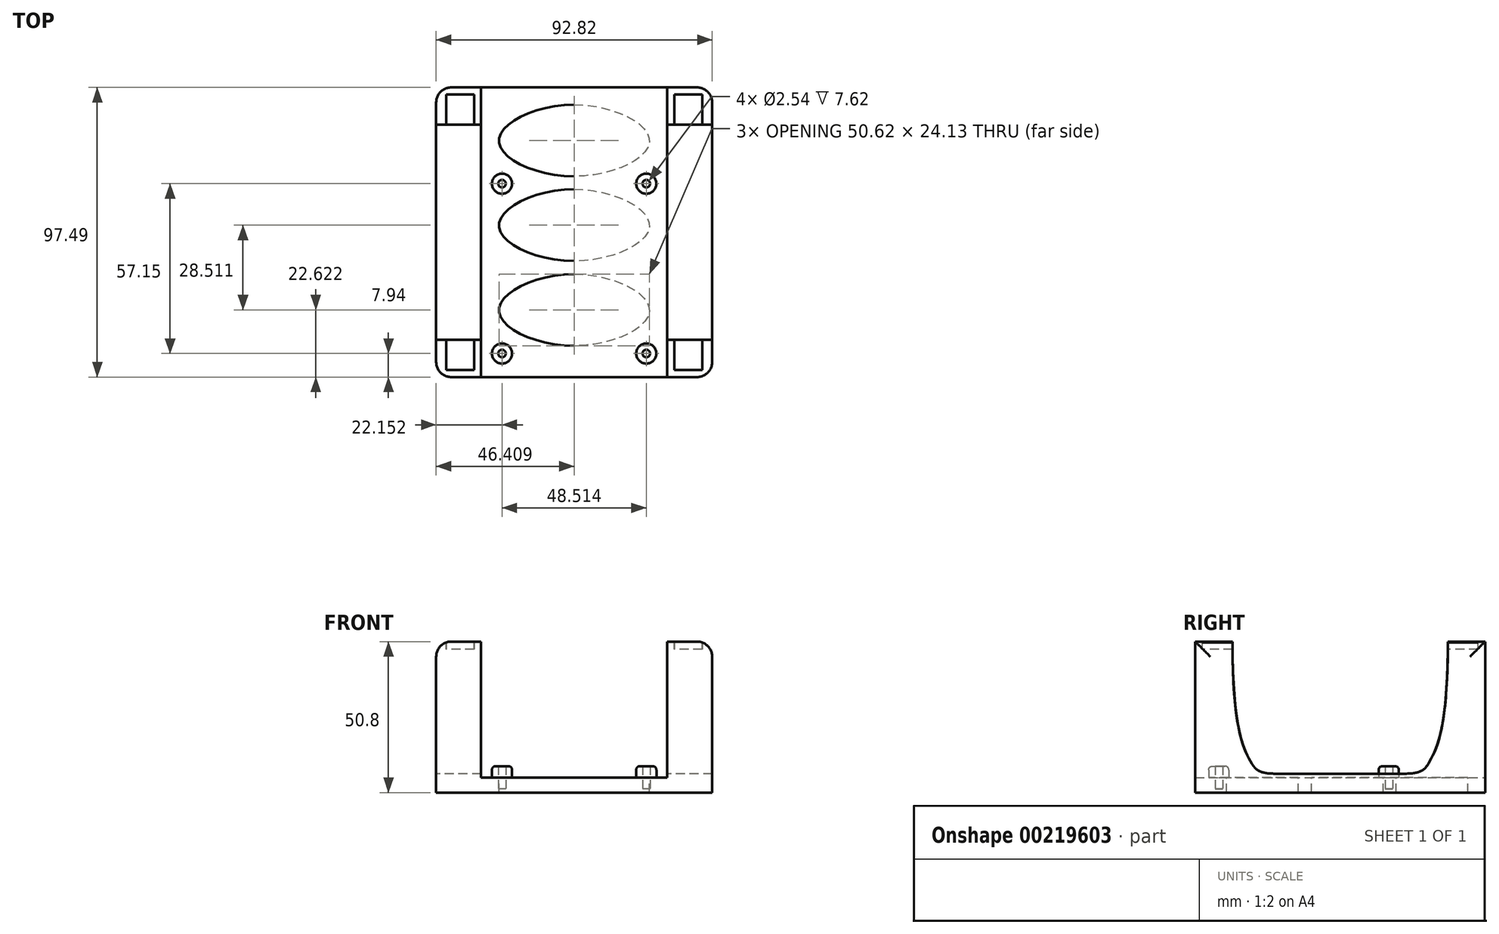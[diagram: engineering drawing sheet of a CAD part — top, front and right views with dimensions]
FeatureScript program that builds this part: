
annotation { "Feature Type Name" : "Feature", "Feature Type Description" : "" }
export const myFeature = defineFeature(function(context is Context, id is Id, definition is map)
    precondition{}
    {
        {
            var Q0;
            Q0=qCreatedBy(makeId("Top.planeOp"),FACE);
            var sketch = newSketch(context, id + "F0", { "sketchPlane" : qUnion([Q0])});
            skLineSegment(sketch, "E0.bottom", {"start": v(0, 8.91) * mm, "end": v(92.82, 8.91) * mm});
            skLineSegment(sketch, "E0.top", {"start": v(0, 106.4) * mm, "end": v(92.82, 106.4) * mm});
            skLineSegment(sketch, "E0.left", {"start": v(0, 8.91) * mm, "end": v(0, 106.4) * mm});
            skLineSegment(sketch, "E0.right", {"start": v(92.82, 8.91) * mm, "end": v(92.82, 106.4) * mm});
            skLineSegment(sketch, "E1.bottom", {"start": v(3.36, 104.01) * mm, "end": v(12.75, 104.01) * mm});
            skLineSegment(sketch, "E1.top", {"start": v(3.36, 11.3) * mm, "end": v(12.75, 11.3) * mm});
            skLineSegment(sketch, "E1.left", {"start": v(3.36, 104.01) * mm, "end": v(3.36, 11.3) * mm});
            skLineSegment(sketch, "E1.right", {"start": v(12.75, 104.01) * mm, "end": v(12.75, 11.3) * mm});
            skLineSegment(sketch, "E2", {"start": v(46.4, 106.4) * mm, "end": v(46.4, 8.91) * mm, "construction": true});
            skLineSegment(sketch, "E3", {"start": v(12.75, 11.3) * mm, "end": v(12.75, 8.91) * mm, "construction": true});
            skLineSegment(sketch, "E4", {"start": v(12.75, 104.01) * mm, "end": v(12.75, 106.4) * mm, "construction": true});
            skLineSegment(sketch, "E5.MirrorCS", {"start": v(89.46, 104.01) * mm, "end": v(80.06, 104.01) * mm});
            skLineSegment(sketch, "E6.MirrorCS", {"start": v(80.06, 104.01) * mm, "end": v(80.06, 11.3) * mm});
            skLineSegment(sketch, "E7.MirrorCS", {"start": v(89.46, 104.01) * mm, "end": v(89.46, 11.3) * mm});
            skLineSegment(sketch, "E8.MirrorCS", {"start": v(89.46, 11.3) * mm, "end": v(80.06, 11.3) * mm});
            skSolve(sketch);
        }
        {
            var Q0;
            Q0=makeQuery(id+"F0.imprint","IMPRINT",FACE,{"disambiguationData":[TD([[makeQuery(id+"F0.imprint","IMPRINT",EDGE,{"derivedFrom":sQuery(id+"F0.wireOp",EDGE,"E0.bottom")}),1.0]])]});
            var Q1;
            Q1=makeQuery(id+"F0.imprint","IMPRINT",FACE,{"disambiguationData":[TD([[makeQuery(id+"F0.imprint","IMPRINT",EDGE,{"derivedFrom":sQuery(id+"F0.wireOp",EDGE,"E1.bottom")}),-1.0]])]});
            var Q2;
            Q2=makeQuery(id+"F0.imprint","IMPRINT",FACE,{"disambiguationData":[TD([[makeQuery(id+"F0.imprint","IMPRINT",EDGE,{"derivedFrom":sQuery(id+"F0.wireOp",EDGE,"E5.MirrorCS")}),1.0]])]});
            extrude(context, id + "F1", {"entities" : qUnion([Q0, Q1, Q2]), "oppositeDirection" : true, "depth" : 50.8 * mm});
        }
        {
            var Q0;
            Q0=makeQuery(id+"F0.imprint","IMPRINT",FACE,{"disambiguationData":[TD([[makeQuery(id+"F0.imprint","IMPRINT",EDGE,{"derivedFrom":sQuery(id+"F0.wireOp",EDGE,"E1.bottom")}),-1.0]])]});
            var Q1;
            Q1=makeQuery(id+"F0.imprint","IMPRINT",FACE,{"disambiguationData":[TD([[makeQuery(id+"F0.imprint","IMPRINT",EDGE,{"derivedFrom":sQuery(id+"F0.wireOp",EDGE,"E5.MirrorCS")}),1.0]])]});
            extrude(context, id + "F2", {"entities" : qUnion([Q0, Q1]), "operationType" : NewBodyOperationType.REMOVE, "oppositeDirection" : true, "depth" : 2.54 * mm});
        }
        {
            var Q0;
            Q0=makeQuery(id+"F0.imprint","IMPRINT",FACE,{"disambiguationData":[TD([[makeQuery(id+"F0.imprint","IMPRINT",EDGE,{"derivedFrom":sQuery(id+"F0.wireOp",EDGE,"E0.bottom")}),1.0]])]});
            var sketch = newSketch(context, id + "F3", { "sketchPlane" : qUnion([Q0])});
            skLineSegment(sketch, "E9.bottom", {"start": v(77.71, 8.91) * mm, "end": v(15.1, 8.91) * mm});
            skLineSegment(sketch, "E9.top", {"start": v(77.71, 106.4) * mm, "end": v(15.1, 106.4) * mm});
            skLineSegment(sketch, "E9.left", {"start": v(77.71, 8.91) * mm, "end": v(77.71, 106.4) * mm});
            skLineSegment(sketch, "E9.right", {"start": v(15.1, 8.91) * mm, "end": v(15.1, 106.4) * mm});
            skPoint(sketch, "E9.middle", {"position": v(46.4, 57.66) * mm});
            skSolve(sketch);
        }
        {
            var Q0;
            Q0=makeQuery(id+"F3.imprint","IMPRINT",FACE,{"disambiguationData":[TD([[makeQuery(id+"F3.imprint","IMPRINT",EDGE,{"derivedFrom":sQuery(id+"F3.wireOp",EDGE,"E9.bottom")}),1.0]])]});
            extrude(context, id + "F4", {"entities" : qUnion([Q0]), "operationType" : NewBodyOperationType.REMOVE, "oppositeDirection" : true, "depth" : 45.72 * mm});
        }
        {
            var Q0;
            Q0=makeQuery(id+"F1.opExtrude","SWEPT_FACE",FACE,{"disambiguationData":[OSD([sQuery(id+"F0.wireOp",EDGE,"E0.left")])]});
            var sketch = newSketch(context, id + "F5", { "sketchPlane" : qUnion([Q0])});
            skPoint(sketch, "E10", {"position": v(-57.66, 0) * mm});
            skLineSegment(sketch, "E11", {"start": v(-93.85, 0) * mm, "end": v(-21.46, 0) * mm, "construction": true});
            skPoint(sketch, "E12", {"position": v(-104.01, 0) * mm});
            skFitSpline(sketch, "E13", {"points": [v(-93.85, 0) * mm, v(-87.7, -40.47) * mm, v(-79.46, -44.45) * mm], "startDerivative": vector(0, -127.08) * mm, "endDerivative": vector(55.42, 0) * mm});
            skLineSegment(sketch, "E14", {"start": v(-79.46, -44.45) * mm, "end": v(-57.66, -44.45) * mm});
            skLineSegment(sketch, "E15", {"start": v(-57.66, 0) * mm, "end": v(-57.66, -44.45) * mm, "construction": true});
            skLineSegment(sketch, "E16.MirrorCS", {"start": v(-35.86, -44.45) * mm, "end": v(-57.66, -44.45) * mm});
            skFitSpline(sketch, "E17.MirrorCS", {"points": [v(-21.46, 0) * mm, v(-27.62, -40.47) * mm, v(-35.86, -44.45) * mm], "startDerivative": vector(0, -127.08) * mm, "endDerivative": vector(-55.42, 0) * mm});
            skLineSegment(sketch, "E18", {"start": v(-93.85, 0) * mm, "end": v(-21.46, 0) * mm});
            skSolve(sketch);
        }
        {
            var Q0;
            {var subQ0=sQuery(id+"F5.wireOp",EDGE,"dd278821-00e8-4460-ae2d-502975557ae5");Q0=makeQuery(id+"F5.imprint","IMPRINT",FACE,{"disambiguationData":[TD([[makeQuery(id+"F5.imprint","IMPRINT",EDGE,{"derivedFrom":subQ0}),1.0]])]});}
            var Q1;
            Q1=makeQuery(id+"F5.imprint","IMPRINT",FACE,{"disambiguationData":[TD([[makeQuery(id+"F5.imprint","IMPRINT",EDGE,{"derivedFrom":sQuery(id+"F5.wireOp",EDGE,"E13")}),1.0]])]});
            extrude(context, id + "F6", {"entities" : qUnion([Q0, Q1]), "operationType" : NewBodyOperationType.REMOVE, "endBound" : BoundingType.THROUGH_ALL, "oppositeDirection" : true, "depth" : 25.4 * mm});
        }
        {
            var Q0;
            Q0=makeQuery(id+"F4.boolean.opBoolean","COPY",FACE,{"derivedFrom":makeQuery(id+"F4.opExtrude","CAP_FACE",FACE,{"disambiguationData":[OSD([sQuery(id+"F3.wireOp",EDGE,"E9.bottom"),sQuery(id+"F3.wireOp",EDGE,"E9.top"),sQuery(id+"F3.wireOp",EDGE,"E9.left"),sQuery(id+"F3.wireOp",EDGE,"E9.right")])],"isStart":false})});
            var sketch = newSketch(context, id + "F7", { "sketchPlane" : qUnion([Q0])});
            skLineSegment(sketch, "E19.bottom", {"start": v(18.34, 77.81) * mm, "end": v(74.48, 77.81) * mm});
            skLineSegment(sketch, "E19.top", {"start": v(18.34, -9.31) * mm, "end": v(74.48, -9.31) * mm});
            skLineSegment(sketch, "E19.left", {"start": v(18.34, 77.81) * mm, "end": v(18.34, -9.31) * mm});
            skLineSegment(sketch, "E19.right", {"start": v(74.48, 77.81) * mm, "end": v(74.48, -9.31) * mm});
            skCircle(sketch, "E20", {"center": v(22.15, 74) * mm, "radius": 1.27 * mm});
            skCircle(sketch, "E21", {"center": v(70.67, 74) * mm, "radius": 1.27 * mm});
            skLineSegment(sketch, "E22", {"start": v(22.15, 74) * mm, "end": v(70.67, 74) * mm, "construction": true});
            skLineSegment(sketch, "E23", {"start": v(22.15, 74) * mm, "end": v(18.34, 74) * mm, "construction": true});
            skLineSegment(sketch, "E24", {"start": v(70.67, 74) * mm, "end": v(74.48, 74) * mm, "construction": true});
            skLineSegment(sketch, "E25", {"start": v(70.67, 74) * mm, "end": v(70.67, 77.81) * mm, "construction": true});
            skCircle(sketch, "E26", {"center": v(70.67, 16.85) * mm, "radius": 1.27 * mm});
            skLineSegment(sketch, "E27", {"start": v(70.67, 74) * mm, "end": v(70.67, 16.85) * mm, "construction": true});
            skCircle(sketch, "E28", {"center": v(22.15, 16.85) * mm, "radius": 1.27 * mm});
            skPoint(sketch, "E29", {"position": v(46.4, 77.81) * mm});
            skCircle(sketch, "E30", {"center": v(70.67, 74) * mm, "radius": 3.4 * mm});
            skCircle(sketch, "E31", {"center": v(70.67, 16.85) * mm, "radius": 3.4 * mm});
            skCircle(sketch, "E32", {"center": v(22.15, 16.85) * mm, "radius": 3.4 * mm});
            skCircle(sketch, "E33", {"center": v(22.15, 74) * mm, "radius": 3.4 * mm});
            skSolve(sketch);
        }
        {
            var Q0;
            Q0=makeQuery(id+"F7.imprint","IMPRINT",FACE,{"disambiguationData":[TD([[makeQuery(id+"F7.imprint","IMPRINT",EDGE,{"derivedFrom":sQuery(id+"F7.wireOp",EDGE,"E21")}),-1.0]])]});
            var Q1;
            Q1=makeQuery(id+"F7.imprint","IMPRINT",FACE,{"disambiguationData":[TD([[makeQuery(id+"F7.imprint","IMPRINT",EDGE,{"derivedFrom":sQuery(id+"F7.wireOp",EDGE,"E20")}),-1.0]])]});
            var Q2;
            Q2=makeQuery(id+"F7.imprint","IMPRINT",FACE,{"disambiguationData":[TD([[makeQuery(id+"F7.imprint","IMPRINT",EDGE,{"derivedFrom":sQuery(id+"F7.wireOp",EDGE,"E28")}),-1.0]])]});
            var Q3;
            Q3=makeQuery(id+"F7.imprint","IMPRINT",FACE,{"disambiguationData":[TD([[makeQuery(id+"F7.imprint","IMPRINT",EDGE,{"derivedFrom":sQuery(id+"F7.wireOp",EDGE,"E26")}),-1.0]])]});
            extrude(context, id + "F8", {"entities" : qUnion([Q0, Q1, Q2, Q3]), "operationType" : NewBodyOperationType.ADD, "depth" : 3.8 * mm});
        }
        {
            var Q0;
            Q0=makeQuery(id+"F7.imprint","IMPRINT",FACE,{"disambiguationData":[TD([[makeQuery(id+"F7.imprint","IMPRINT",EDGE,{"derivedFrom":sQuery(id+"F7.wireOp",EDGE,"E21")}),1.0]])]});
            var Q1;
            Q1=makeQuery(id+"F7.imprint","IMPRINT",FACE,{"disambiguationData":[TD([[makeQuery(id+"F7.imprint","IMPRINT",EDGE,{"derivedFrom":sQuery(id+"F7.wireOp",EDGE,"E28")}),1.0]])]});
            var Q2;
            Q2=makeQuery(id+"F7.imprint","IMPRINT",FACE,{"disambiguationData":[TD([[makeQuery(id+"F7.imprint","IMPRINT",EDGE,{"derivedFrom":sQuery(id+"F7.wireOp",EDGE,"E20")}),1.0]])]});
            var Q3;
            Q3=makeQuery(id+"F7.imprint","IMPRINT",FACE,{"disambiguationData":[TD([[makeQuery(id+"F7.imprint","IMPRINT",EDGE,{"derivedFrom":sQuery(id+"F7.wireOp",EDGE,"E26")}),1.0]])]});
            extrude(context, id + "F9", {"entities" : qUnion([Q0, Q1, Q2, Q3]), "operationType" : NewBodyOperationType.REMOVE, "oppositeDirection" : true, "depth" : 3.8 * mm});
        }
        {
            var Q0;
            Q0=makeQuery(id+"F1.opExtrude","SWEPT_EDGE",EDGE,{"disambiguationData":[OSD([sQuery(id+"F0.wireOp",EDGE,"E0.bottom"),sQuery(id+"F0.wireOp",EDGE,"E0.left")])]});
            var Q1;
            Q1=makeQuery(id+"F1.opExtrude","SWEPT_EDGE",EDGE,{"disambiguationData":[OSD([sQuery(id+"F0.wireOp",EDGE,"E0.bottom"),sQuery(id+"F0.wireOp",EDGE,"E0.right")])]});
            var Q2;
            Q2=makeQuery(id+"F1.opExtrude","SWEPT_EDGE",EDGE,{"disambiguationData":[OSD([sQuery(id+"F0.wireOp",EDGE,"E0.top"),sQuery(id+"F0.wireOp",EDGE,"E0.left")])]});
            var Q3;
            Q3=makeQuery(id+"F1.opExtrude","SWEPT_EDGE",EDGE,{"disambiguationData":[OSD([sQuery(id+"F0.wireOp",EDGE,"E0.top"),sQuery(id+"F0.wireOp",EDGE,"E0.right")])]});
            var Q4;
            {var subQ0=sQuery(id+"F0.wireOp",EDGE,"E0.bottom");var subQ1=sQuery(id+"F0.wireOp",EDGE,"E0.left");Q4=makeQuery(id+"F6.boolean.opBoolean","SPLIT",EDGE,{"disambiguationData":[TD([makeQuery(id+"F1.opExtrude","SWEPT_FACE",FACE,{"disambiguationData":[OSD([subQ0])]})])],"derivedFrom":makeQuery(id+"F1.opExtrude","CAP_EDGE",EDGE,{"disambiguationData":[OSD([subQ1])],"isStart":true})});}
            var Q5;
            {var subQ0=sQuery(id+"F0.wireOp",EDGE,"E0.left");var subQ1=sQuery(id+"F0.wireOp",EDGE,"E0.top");Q5=makeQuery(id+"F6.boolean.opBoolean","SPLIT",EDGE,{"disambiguationData":[TD([makeQuery(id+"F1.opExtrude","SWEPT_FACE",FACE,{"disambiguationData":[OSD([subQ1])]})])],"derivedFrom":makeQuery(id+"F1.opExtrude","CAP_EDGE",EDGE,{"disambiguationData":[OSD([subQ0])],"isStart":true})});}
            var Q6;
            {var subQ0=sQuery(id+"F0.wireOp",EDGE,"E0.right");var subQ1=sQuery(id+"F0.wireOp",EDGE,"E0.top");Q6=makeQuery(id+"F6.boolean.opBoolean","SPLIT",EDGE,{"disambiguationData":[TD([makeQuery(id+"F1.opExtrude","SWEPT_FACE",FACE,{"disambiguationData":[OSD([subQ1])]})])],"derivedFrom":makeQuery(id+"F1.opExtrude","CAP_EDGE",EDGE,{"disambiguationData":[OSD([subQ0])],"isStart":true})});}
            var Q7;
            {var subQ0=sQuery(id+"F0.wireOp",EDGE,"E0.bottom");var subQ1=sQuery(id+"F0.wireOp",EDGE,"E0.right");Q7=makeQuery(id+"F6.boolean.opBoolean","SPLIT",EDGE,{"disambiguationData":[TD([makeQuery(id+"F1.opExtrude","SWEPT_FACE",FACE,{"disambiguationData":[OSD([subQ0])]})])],"derivedFrom":makeQuery(id+"F1.opExtrude","CAP_EDGE",EDGE,{"disambiguationData":[OSD([subQ1])],"isStart":true})});}
            var Q8;
            Q8=makeQuery(id+"F6.boolean.opBoolean","COPY",EDGE,{"derivedFrom":makeQuery(id+"F6.opExtrude","CAP_EDGE",EDGE,{"disambiguationData":[OSD([sQuery(id+"F5.wireOp",EDGE,"dd278821-00e8-4460-ae2d-502975557ae5")])],"isStart":true})});
            var Q9;
            Q9=makeQuery(id+"F6.boolean.opBoolean","INTERSECT",EDGE,{"derivedFrom":[makeQuery(id+"F1.opExtrude","SWEPT_FACE",FACE,{"disambiguationData":[OSD([sQuery(id+"F0.wireOp",EDGE,"E0.right")])]}),makeQuery(id+"F6.opExtrude","SWEPT_FACE",FACE,{"disambiguationData":[OSD([sQuery(id+"F5.wireOp",EDGE,"dd278821-00e8-4460-ae2d-502975557ae5")])]})]});
            var Q10;
            Q10=makeQuery(id+"F4.boolean.opBoolean","COPY",EDGE,{"derivedFrom":makeQuery(id+"F4.opExtrude","SWEPT_EDGE",EDGE,{"disambiguationData":[OSD([sQuery(id+"F0.wireOp",EDGE,"E0.top"),sQuery(id+"F3.wireOp",EDGE,"E9.top"),sQuery(id+"F3.wireOp",EDGE,"E9.left")])]})});
            var Q11;
            Q11=makeQuery(id+"F4.boolean.opBoolean","COPY",EDGE,{"derivedFrom":makeQuery(id+"F4.opExtrude","SWEPT_EDGE",EDGE,{"disambiguationData":[OSD([sQuery(id+"F0.wireOp",EDGE,"E0.top"),sQuery(id+"F3.wireOp",EDGE,"E9.top"),sQuery(id+"F3.wireOp",EDGE,"E9.right")])]})});
            var Q12;
            Q12=makeQuery(id+"F4.boolean.opBoolean","COPY",EDGE,{"derivedFrom":makeQuery(id+"F4.opExtrude","SWEPT_EDGE",EDGE,{"disambiguationData":[OSD([sQuery(id+"F0.wireOp",EDGE,"E0.bottom"),sQuery(id+"F3.wireOp",EDGE,"E9.bottom"),sQuery(id+"F3.wireOp",EDGE,"E9.right")])]})});
            var Q13;
            Q13=makeQuery(id+"F4.boolean.opBoolean","COPY",EDGE,{"derivedFrom":makeQuery(id+"F4.opExtrude","SWEPT_EDGE",EDGE,{"disambiguationData":[OSD([sQuery(id+"F0.wireOp",EDGE,"E0.bottom"),sQuery(id+"F3.wireOp",EDGE,"E9.bottom"),sQuery(id+"F3.wireOp",EDGE,"E9.left")])]})});
            var Q14;
            Q14=makeQuery(id+"F6.boolean.opBoolean","COPY",EDGE,{"derivedFrom":makeQuery(id+"F6.opExtrude","CAP_EDGE",EDGE,{"disambiguationData":[OSD([sQuery(id+"F5.wireOp",EDGE,"E14"),sQuery(id+"F5.wireOp",EDGE,"E16.MirrorCS")])],"isStart":true})});
            fillet(context, id + "F10", {"entities" : qUnion([Q0, Q1, Q2, Q3, Q4, Q5, Q6, Q7, Q8, Q9, Q10, Q11, Q12, Q13, Q14]), "radius" : 5.08 * mm, "tangentPropagation" : true, "allowEdgeOverflow" : false});
        }
        {
            var Q0;
            {var subQ1=sQuery(id+"F7.wireOp",EDGE,"E19.bottom");Q0=makeQuery(id+"F7.imprint","IMPRINT",FACE,{"disambiguationData":[TD([[makeQuery(id+"F7.imprint","IMPRINT",EDGE,{"derivedFrom":subQ1}),1.0]])]});}
            var sketch = newSketch(context, id + "F11", { "sketchPlane" : qUnion([Q0])});
            skFitSpline(sketch, "E34", {"points": [v(46.4, 100.62) * mm, v(71.72, 88.55) * mm, v(46.4, 76.49) * mm], "startDerivative": vector(75.9, 0) * mm, "endDerivative": vector(-79.21, 0) * mm});
            skLineSegment(sketch, "E35", {"start": v(46.4, 100.62) * mm, "end": v(46.4, 76.49) * mm, "construction": true});
            skFitSpline(sketch, "E36.MirrorCS", {"points": [v(46.4, 100.62) * mm, v(21.1, 88.55) * mm, v(46.4, 76.49) * mm], "startDerivative": vector(-75.9, 0) * mm, "endDerivative": vector(79.21, 0) * mm});
            skFitSpline(sketch, "E37", {"points": [v(46.4, 72.1) * mm, v(71.72, 60.04) * mm, v(46.4, 47.98) * mm], "startDerivative": vector(75.94, 0) * mm, "endDerivative": vector(-79.25, 0) * mm});
            skLineSegment(sketch, "E38", {"start": v(46.4, 72.1) * mm, "end": v(46.4, 47.98) * mm, "construction": true});
            skFitSpline(sketch, "E39.MirrorCS", {"points": [v(46.4, 72.1) * mm, v(21.1, 60.04) * mm, v(46.4, 47.98) * mm], "startDerivative": vector(-75.94, 0) * mm, "endDerivative": vector(79.25, 0) * mm});
            skFitSpline(sketch, "E40", {"points": [v(46.4, 43.6) * mm, v(71.72, 31.53) * mm, v(46.4, 19.46) * mm], "startDerivative": vector(75.86, 0) * mm, "endDerivative": vector(-79.18, 0) * mm});
            skLineSegment(sketch, "E41", {"start": v(46.4, 43.6) * mm, "end": v(46.4, 19.46) * mm, "construction": true});
            skFitSpline(sketch, "E42.MirrorCS", {"points": [v(46.4, 43.6) * mm, v(21.1, 31.53) * mm, v(46.4, 19.46) * mm], "startDerivative": vector(-75.86, 0) * mm, "endDerivative": vector(79.18, 0) * mm});
            skLineSegment(sketch, "E43", {"start": v(46.4, 76.49) * mm, "end": v(46.4, 72.1) * mm, "construction": true});
            skLineSegment(sketch, "E44", {"start": v(46.4, 47.98) * mm, "end": v(46.4, 43.6) * mm, "construction": true});
            skLineSegment(sketch, "E45", {"start": v(71.72, 88.55) * mm, "end": v(71.72, 60.04) * mm, "construction": true});
            skLineSegment(sketch, "E46", {"start": v(71.72, 60.04) * mm, "end": v(71.72, 31.53) * mm, "construction": true});
            skLineSegment(sketch, "E47", {"start": v(21.1, 31.53) * mm, "end": v(21.1, 60.04) * mm, "construction": true});
            skLineSegment(sketch, "E48", {"start": v(21.1, 60.04) * mm, "end": v(21.1, 88.55) * mm, "construction": true});
            skLineSegment(sketch, "E49", {"start": v(46.4, 100.62) * mm, "end": v(46.4, 106.4) * mm, "construction": true});
            skLineSegment(sketch, "E50", {"start": v(46.4, 19.46) * mm, "end": v(46.4, 8.91) * mm, "construction": true});
            skLineSegment(sketch, "E51", {"start": v(21.1, 88.55) * mm, "end": v(71.72, 88.55) * mm, "construction": true});
            skLineSegment(sketch, "E52", {"start": v(71.72, 60.04) * mm, "end": v(21.1, 60.04) * mm, "construction": true});
            skLineSegment(sketch, "E53", {"start": v(21.1, 31.53) * mm, "end": v(71.72, 31.53) * mm, "construction": true});
            skPoint(sketch, "E54", {"position": v(46.4, 88.55) * mm});
            skPoint(sketch, "E55", {"position": v(46.4, 60.04) * mm});
            skPoint(sketch, "E56", {"position": v(46.4, 31.53) * mm});
            skSolve(sketch);
        }
        {
            var Q0;
            Q0 = qSketchRegion(id + "F11", true);
            extrude(context, id + "F12", {"entities" : qUnion([Q0]), "operationType" : NewBodyOperationType.REMOVE, "endBound" : BoundingType.THROUGH_ALL, "oppositeDirection" : true, "depth" : 25.4 * mm});
        }
        {
            var Q0;
            Q0=makeQuery(id+"F8.opExtrude","CAP_EDGE",EDGE,{"disambiguationData":[OSD([sQuery(id+"F7.wireOp",EDGE,"E32")])],"isStart":true});
            var Q1;
            Q1=makeQuery(id+"F8.opExtrude","CAP_EDGE",EDGE,{"disambiguationData":[OSD([sQuery(id+"F7.wireOp",EDGE,"E33")])],"isStart":true});
            var Q2;
            Q2=makeQuery(id+"F8.opExtrude","CAP_EDGE",EDGE,{"disambiguationData":[OSD([sQuery(id+"F7.wireOp",EDGE,"E33")])],"isStart":false});
            var Q3;
            Q3=makeQuery(id+"F8.opExtrude","CAP_EDGE",EDGE,{"disambiguationData":[OSD([sQuery(id+"F7.wireOp",EDGE,"E32")])],"isStart":false});
            var Q4;
            Q4=makeQuery(id+"F8.opExtrude","CAP_EDGE",EDGE,{"disambiguationData":[OSD([sQuery(id+"F7.wireOp",EDGE,"E31")])],"isStart":false});
            var Q5;
            Q5=makeQuery(id+"F8.opExtrude","CAP_EDGE",EDGE,{"disambiguationData":[OSD([sQuery(id+"F7.wireOp",EDGE,"E31")])],"isStart":true});
            var Q6;
            Q6=makeQuery(id+"F8.opExtrude","CAP_EDGE",EDGE,{"disambiguationData":[OSD([sQuery(id+"F7.wireOp",EDGE,"E30")])],"isStart":true});
            var Q7;
            Q7=makeQuery(id+"F8.opExtrude","CAP_EDGE",EDGE,{"disambiguationData":[OSD([sQuery(id+"F7.wireOp",EDGE,"E30")])],"isStart":false});
            var Q8;
            Q8=makeQuery(id+"F12.boolean.opBoolean","COPY",EDGE,{"derivedFrom":makeQuery(id+"F12.opExtrude","CAP_EDGE",EDGE,{"disambiguationData":[OSD([sQuery(id+"F11.wireOp",EDGE,"E36.MirrorCS")])],"isStart":true})});
            var Q9;
            Q9=makeQuery(id+"F12.boolean.opBoolean","COPY",EDGE,{"derivedFrom":makeQuery(id+"F12.opExtrude","CAP_EDGE",EDGE,{"disambiguationData":[OSD([sQuery(id+"F11.wireOp",EDGE,"E39.MirrorCS")])],"isStart":true})});
            var Q10;
            Q10=makeQuery(id+"F12.boolean.opBoolean","COPY",EDGE,{"derivedFrom":makeQuery(id+"F12.opExtrude","CAP_EDGE",EDGE,{"disambiguationData":[OSD([sQuery(id+"F11.wireOp",EDGE,"E40")])],"isStart":true})});
            fillet(context, id + "F13", {"entities" : qUnion([Q0, Q1, Q2, Q3, Q4, Q5, Q6, Q7, Q8, Q9, Q10]), "radius" : 1.27 * mm, "tangentPropagation" : true, "allowEdgeOverflow" : false});
        }
    });
